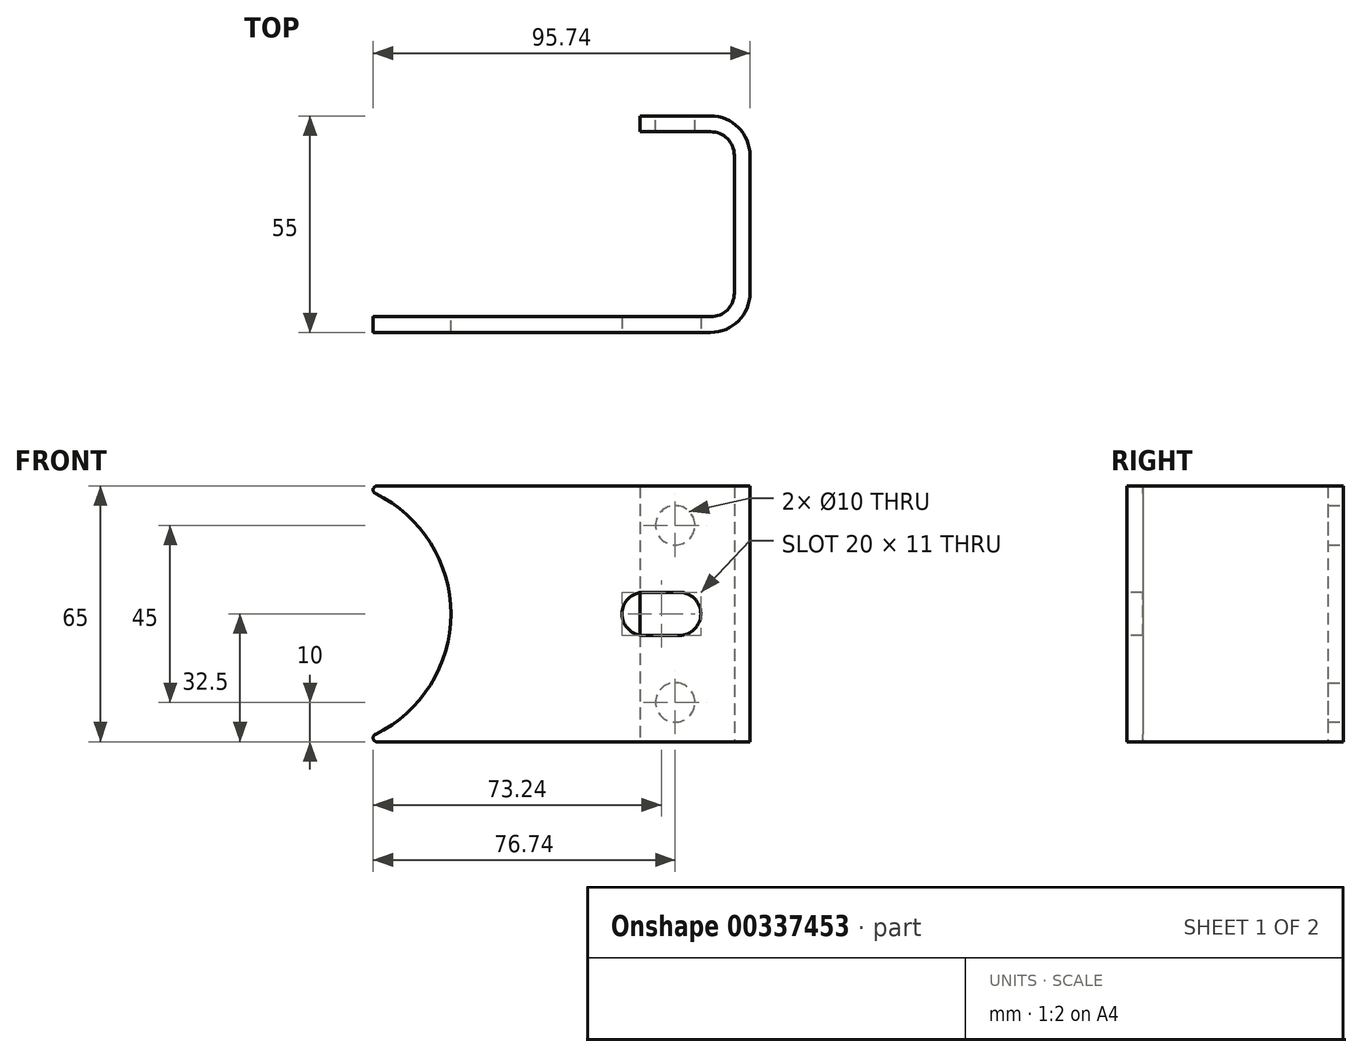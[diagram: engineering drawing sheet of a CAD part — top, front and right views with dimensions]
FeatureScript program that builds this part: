
annotation { "Feature Type Name" : "Feature", "Feature Type Description" : "" }
export const myFeature = defineFeature(function(context is Context, id is Id, definition is map)
    precondition{}
    {
        {
            var Q0;
            Q0=qCreatedBy(makeId("Top.planeOp"),FACE);
            var sketch = newSketch(context, id + "F0", { "sketchPlane" : qUnion([Q0])});
            skLineSegment(sketch, "E0", {"start": v(0, 10) * mm, "end": v(0, 45) * mm});
            skLineSegment(sketch, "E1", {"start": v(-10, 55) * mm, "end": v(-28, 55) * mm});
            skLineSegment(sketch, "E2", {"start": v(-28, 55) * mm, "end": v(-28, 51) * mm});
            skPoint(sketch, "E3.visualSharp", {"position": v(0, 55) * mm});
            skArc(sketch, "E3.filletArc", {"start": v(0, 45) * mm, "mid": v(-2.93, 52.07) * mm, "end": v(-10, 55) * mm});
            skLineSegment(sketch, "E4", {"start": v(-28, 51) * mm, "end": v(-10, 51) * mm});
            skLineSegment(sketch, "E5", {"start": v(-4, 45) * mm, "end": v(-4, 10) * mm});
            skPoint(sketch, "E6.visualSharp", {"position": v(-4, 51) * mm});
            skArc(sketch, "E6.filletArc", {"start": v(-4, 45) * mm, "mid": v(-5.76, 49.24) * mm, "end": v(-10, 51) * mm});
            skLineSegment(sketch, "E7", {"start": v(-10, 0) * mm, "end": v(-110, 0) * mm});
            skLineSegment(sketch, "E8", {"start": v(-110, 0) * mm, "end": v(-110, 4) * mm});
            skLineSegment(sketch, "E9", {"start": v(-110, 4) * mm, "end": v(-10, 4) * mm});
            skPoint(sketch, "E10.visualSharp", {"position": v(0, 0) * mm});
            skArc(sketch, "E10.filletArc", {"start": v(-10, 0) * mm, "mid": v(-2.93, 2.93) * mm, "end": v(0, 10) * mm});
            skPoint(sketch, "E11.visualSharp", {"position": v(-4, 4) * mm});
            skArc(sketch, "E11.filletArc", {"start": v(-10, 4) * mm, "mid": v(-5.76, 5.76) * mm, "end": v(-4, 10) * mm});
            skSolve(sketch);
        }
        {
            var Q0;
            Q0 = qSketchRegion(id + "F0", true);
            extrude(context, id + "F1", {"entities" : qUnion([Q0]), "depth" : 65 * mm});
        }
        {
            var Q0;
            Q0=makeQuery(id+"F1.opExtrude","SWEPT_FACE",FACE,{"disambiguationData":[OSD([sQuery(id+"F0.wireOp",EDGE,"E9")])]});
            cPlane(context, id + "F2", {"entities" : qUnion([Q0]), "cplaneType" : CPlaneType.OFFSET, "offset" : 0 * mm, "width" : 150 * mm, "height" : 150 * mm});
        }
        {
            var Q0;
            Q0=qCreatedBy(id+"F2.planeOp",FACE);
            var sketch = newSketch(context, id + "F3", { "sketchPlane" : qUnion([Q0])});
            skCircle(sketch, "E12", {"center": v(110, 32.5) * mm, "radius": 34 * mm});
            skSolve(sketch);
        }
        {
            var Q0;
            Q0 = qSketchRegion(id + "F3", true);
            extrude(context, id + "F4", {"entities" : qUnion([Q0]), "operationType" : NewBodyOperationType.REMOVE, "oppositeDirection" : true, "depth" : 25 * mm});
        }
        {
            var Q0;
            Q0=makeQuery(id+"F4.boolean.opBoolean","INTERSECT",EDGE,{"derivedFrom":[makeQuery(id+"F1.opExtrude","CAP_FACE",FACE,{"disambiguationData":[OSD([sQuery(id+"F0.wireOp",EDGE,"E0"),sQuery(id+"F0.wireOp",EDGE,"E1"),sQuery(id+"F0.wireOp",EDGE,"E2"),sQuery(id+"F0.wireOp",EDGE,"E3.filletArc"),sQuery(id+"F0.wireOp",EDGE,"E4"),sQuery(id+"F0.wireOp",EDGE,"E5"),sQuery(id+"F0.wireOp",EDGE,"E6.filletArc"),sQuery(id+"F0.wireOp",EDGE,"E7"),sQuery(id+"F0.wireOp",EDGE,"E8"),sQuery(id+"F0.wireOp",EDGE,"E9"),sQuery(id+"F0.wireOp",EDGE,"E10.filletArc"),sQuery(id+"F0.wireOp",EDGE,"E11.filletArc")])],"isStart":false}),makeQuery(id+"F4.opExtrude","SWEPT_FACE",FACE,{"disambiguationData":[OSD([sQuery(id+"F3.wireOp",EDGE,"E12")])]})]});
            var Q1;
            Q1=makeQuery(id+"F4.boolean.opBoolean","INTERSECT",EDGE,{"derivedFrom":[makeQuery(id+"F1.opExtrude","CAP_FACE",FACE,{"disambiguationData":[OSD([sQuery(id+"F0.wireOp",EDGE,"E0"),sQuery(id+"F0.wireOp",EDGE,"E1"),sQuery(id+"F0.wireOp",EDGE,"E2"),sQuery(id+"F0.wireOp",EDGE,"E3.filletArc"),sQuery(id+"F0.wireOp",EDGE,"E4"),sQuery(id+"F0.wireOp",EDGE,"E5"),sQuery(id+"F0.wireOp",EDGE,"E6.filletArc"),sQuery(id+"F0.wireOp",EDGE,"E7"),sQuery(id+"F0.wireOp",EDGE,"E8"),sQuery(id+"F0.wireOp",EDGE,"E9"),sQuery(id+"F0.wireOp",EDGE,"E10.filletArc"),sQuery(id+"F0.wireOp",EDGE,"E11.filletArc")])],"isStart":true}),makeQuery(id+"F4.opExtrude","SWEPT_FACE",FACE,{"disambiguationData":[OSD([sQuery(id+"F3.wireOp",EDGE,"E12")])]})]});
            fillet(context, id + "F5", {"entities" : qUnion([Q0, Q1]), "radius" : 1 * mm, "tangentPropagation" : true, "allowEdgeOverflow" : false});
        }
        {
            var Q0;
            Q0=makeQuery(id+"F1.opExtrude","SWEPT_FACE",FACE,{"disambiguationData":[OSD([sQuery(id+"F0.wireOp",EDGE,"E1")])]});
            cPlane(context, id + "F6", {"entities" : qUnion([Q0]), "cplaneType" : CPlaneType.OFFSET, "offset" : 0 * mm, "width" : 150 * mm, "height" : 150 * mm});
        }
        {
            var Q0;
            Q0=qCreatedBy(id+"F6.planeOp",FACE);
            var sketch = newSketch(context, id + "F7", { "sketchPlane" : qUnion([Q0])});
            skCircle(sketch, "E13", {"center": v(19, 55) * mm, "radius": 5 * mm});
            skCircle(sketch, "E14", {"center": v(19, 10) * mm, "radius": 5 * mm});
            skSolve(sketch);
        }
        {
            var Q0;
            Q0 = qSketchRegion(id + "F7", true);
            extrude(context, id + "F8", {"entities" : qUnion([Q0]), "operationType" : NewBodyOperationType.REMOVE, "oppositeDirection" : true, "depth" : 25 * mm});
        }
        {
            var Q0;
            Q0=makeQuery(id+"F1.opExtrude","SWEPT_FACE",FACE,{"disambiguationData":[OSD([sQuery(id+"F0.wireOp",EDGE,"E7")])]});
            cPlane(context, id + "F9", {"entities" : qUnion([Q0]), "cplaneType" : CPlaneType.OFFSET, "offset" : 0 * mm, "width" : 150 * mm, "height" : 150 * mm});
        }
        {
            var Q0;
            Q0=qCreatedBy(id+"F9.planeOp",FACE);
            var sketch = newSketch(context, id + "F10", { "sketchPlane" : qUnion([Q0])});
            skLineSegment(sketch, "E15", {"start": v(0, 0) * mm, "end": v(0, 32.5) * mm});
            skLineSegment(sketch, "E16", {"start": v(0, 32.5) * mm, "end": v(-22, 32.5) * mm});
            skLineSegment(sketch, "E17", {"start": v(-12.5, 32.5) * mm, "end": v(-12.5, 32.5) * mm});
            skLineSegment(sketch, "E18", {"start": v(-18, 27) * mm, "end": v(-27, 27) * mm});
            skLineSegment(sketch, "E19", {"start": v(-32.5, 32.5) * mm, "end": v(-32.5, 32.5) * mm});
            skLineSegment(sketch, "E20", {"start": v(-27, 38) * mm, "end": v(-18, 38) * mm});
            skPoint(sketch, "E21.visualSharp", {"position": v(-32.5, 27) * mm});
            skArc(sketch, "E21.filletArc", {"start": v(-32.5, 32.5) * mm, "mid": v(-30.89, 28.61) * mm, "end": v(-27, 27) * mm});
            skPoint(sketch, "E22.visualSharp", {"position": v(-32.5, 38) * mm});
            skArc(sketch, "E22.filletArc", {"start": v(-27, 38) * mm, "mid": v(-30.89, 36.39) * mm, "end": v(-32.5, 32.5) * mm});
            skPoint(sketch, "E23.visualSharp", {"position": v(-12.5, 38) * mm});
            skArc(sketch, "E23.filletArc", {"start": v(-12.5, 32.5) * mm, "mid": v(-14.11, 36.39) * mm, "end": v(-18, 38) * mm});
            skPoint(sketch, "E24.visualSharp", {"position": v(-12.5, 27) * mm});
            skArc(sketch, "E24.filletArc", {"start": v(-18, 27) * mm, "mid": v(-14.11, 28.61) * mm, "end": v(-12.5, 32.5) * mm});
            skSolve(sketch);
        }
        {
            var Q0;
            Q0 = qSketchRegion(id + "F10", true);
            extrude(context, id + "F11", {"entities" : qUnion([Q0]), "operationType" : NewBodyOperationType.REMOVE, "oppositeDirection" : true, "depth" : 25 * mm});
        }
    });
